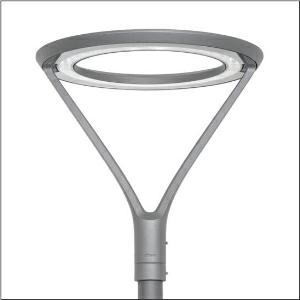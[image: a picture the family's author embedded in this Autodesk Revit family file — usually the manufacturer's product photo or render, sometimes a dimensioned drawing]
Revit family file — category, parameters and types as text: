
# Revit family: dl_r__20___st1_2a_5xa51283wa008p_0b9f
name_source: partatom
category: Lighting Fixtures
units: mm (PartAtom-declared; Revit-internal decimal feet)

## family parameters
Cut with Voids When Loaded = No
Host = Face
Light Source = No
Part Type = Normal
Room Calculation Point = No
Round Connector Dimension = Use Diameter
Shared = No

## types (1)
- --- (1 x LED, 4200 lm, 34.3 W, 3000K)
    Apparent Load = 34 VA
    CIE Flux Codes = 32 72 97 100 100
    Color Rendering = 70
    Color Temperature = 3000K
    Default Elevation = 1800 mm
    Description = DL® 20, mast luminaire, primary light control with reflector, highly specular, primary optical cover: cover, of toughened safety glass of clear glass with excellent transmission level, light distribution: ST1.2a, light emission: direct distribution, primary light characteristic: asymmetric, installation type: post-top, LED, High Power LED, rated luminous flux: 4.180lm, luminous efficacy: 79lm/W, light colour: 730, colour temperature: 3000K, control gear: ECG Plus, control: overheat protection, power reduction, digital communication interface, constant luminous flux control, time-dependent luminous flux control, flexible luminous flux parameterisation, electronic power reduction, mains connection: 230..240V, 50/60Hz, connection cable pre-assembled, cable length: 5m, start of lifetime: 53W, end of service life: 54W, reduction: 24W, luminaire housing, upper part, of cast aluminium, powder-coated, Siteco® metallic grey (DB 702S), diameter: 690mm, height: 690mm, spigot size: 76mm (post-top), luminaire housing, of cast aluminium, powder-coated, Siteco® metallic grey (DB 702S), equipment: Power, protection rating (complete): IP66, insulation class (complete): insulation class II (safety insulation), certification: CE, ENEC, VDE, impact resistance: IK08, permissible operating ambient temperature: -25..+30°C, standard-compliant lighting for roads and squares, packaging unit: 1 piece

Light Distribution: ST1.2a
    Height = 690 mm
    Lamp = 1 x LED
    Lamp Light Flux = 4200 lm
    Lamp Power = 34.3 W
    Lamp count = 1
    Length = 690 mm
    Luminous efficacy = 122 lm/W
    Manufacturer = Siteco
    ModVariant = No
    Model = 5XA51283WA008P
    Number of Poles = 1
    OnlyDefault = Yes
    Power Factor = 1
    Product Name = DL® 20 | ST1.2a
    Product group = mast luminaire | pylon top
    ProductGroupID = 6100
    Protection Class = Protection class II
    Protection Degree = IP 66
    RLX_Detail_Level = 1
    RLX_Emergency_Light_Flux = 0 lm
    RLX_Emergency_Type = 0
    RLX_Emergency_Type_DB = No
    RlxData = <blob elided: 206937 chars, md5=424da845>
    Socket = socket
    Standby Power = 0 W
    System Light Flux = 4200 lm
    System Power = 34 W
    Type Comments = factory setting: luminous flux: 100 % | dim-lin: 254 | 464 mA
    Type Image = l_1006001.jpg
    URL = http://relux.com
    VarID = @adj_046437
    Voltage = 0 V
    Weight = 0.00 kg
    Width = 0 mm  [stored 0 ft]

note: [stored X ft] marks values corroborated as IEEE doubles in the binary element streams (Revit-internal decimal feet)

## geometry (parser evidence)
native form markers: Blend x4, Sweep x12
no freeform markers — native parametric forms only
